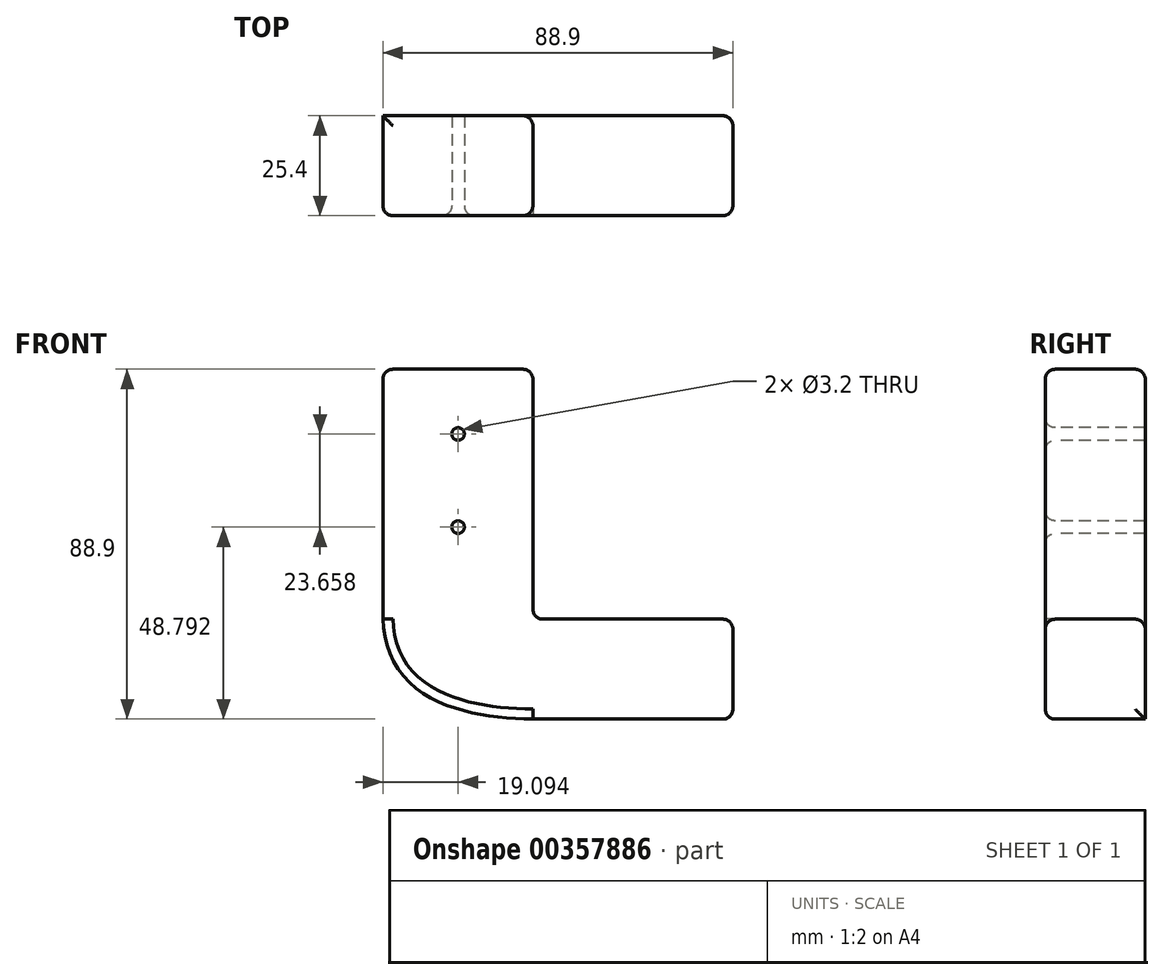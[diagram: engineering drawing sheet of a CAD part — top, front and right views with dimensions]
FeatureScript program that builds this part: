
annotation { "Feature Type Name" : "Feature", "Feature Type Description" : "" }
export const myFeature = defineFeature(function(context is Context, id is Id, definition is map)
    precondition{}
    {
        {
            var Q0;
            Q0=qCreatedBy(makeId("Front.planeOp"),FACE);
            var sketch = newSketch(context, id + "F0", { "sketchPlane" : qUnion([Q0])});
            skLineSegment(sketch, "E0.bottom", {"start": v(-38.1, 63.5) * mm, "end": v(0, 63.5) * mm});
            skLineSegment(sketch, "E0.top", {"start": v(-38.1, 0) * mm, "end": v(0, 0) * mm});
            skLineSegment(sketch, "E0.left", {"start": v(-38.1, 63.5) * mm, "end": v(-38.1, 0) * mm});
            skLineSegment(sketch, "E0.right", {"start": v(0, 63.5) * mm, "end": v(0, 0) * mm});
            skLineSegment(sketch, "E1.bottom", {"start": v(0, 0) * mm, "end": v(50.8, 0) * mm});
            skLineSegment(sketch, "E1.top", {"start": v(0, -25.4) * mm, "end": v(50.8, -25.4) * mm});
            skLineSegment(sketch, "E1.left", {"start": v(0, 0) * mm, "end": v(0, -25.4) * mm});
            skLineSegment(sketch, "E1.right", {"start": v(50.8, 0) * mm, "end": v(50.8, -25.4) * mm});
            skFitSpline(sketch, "E2", {"points": [v(-38.1, 0) * mm, v(0, -25.4) * mm], "startDerivative": vector(1.89, -52.81) * mm, "endDerivative": vector(68.37, -0.94) * mm});
            skSolve(sketch);
        }
        {
            var Q0;
            Q0 = qSketchRegion(id + "F0", true);
            extrude(context, id + "F1", {"entities" : qUnion([Q0]), "depth" : 25.4 * mm});
        }
        {
            var Q0;
            Q0=makeQuery(id+"F1.opExtrude","CAP_FACE",FACE,{"disambiguationData":[OSD([sQuery(id+"F0.wireOp",EDGE,"E0.bottom"),sQuery(id+"F0.wireOp",EDGE,"E0.left"),sQuery(id+"F0.wireOp",EDGE,"E0.right"),sQuery(id+"F0.wireOp",EDGE,"E1.bottom"),sQuery(id+"F0.wireOp",EDGE,"E1.top"),sQuery(id+"F0.wireOp",EDGE,"E1.right"),sQuery(id+"F0.wireOp",EDGE,"E2")])],"isStart":false});
            var sketch = newSketch(context, id + "F2", { "sketchPlane" : qUnion([Q0])});
            skLineSegment(sketch, "E3", {"start": v(-38.1, 63.5) * mm, "end": v(-19, 47.05) * mm});
            skLineSegment(sketch, "E4", {"start": v(-19, 47.05) * mm, "end": v(-19, 23.4) * mm});
            skSolve(sketch);
        }
        {
            var Q0;
            Q0=sQuery(id+"F2.wireOp",VERTEX,"E4.start");
            var Q1;
            Q1=sQuery(id+"F2.wireOp",VERTEX,"E4.end");
            var Q2;
            Q2=makeQuery(id+"F1.opExtrude","SWEPT_BODY",BODY,{"disambiguationData":[OSD([sQuery(id+"F0.wireOp",EDGE,"E0.bottom"),sQuery(id+"F0.wireOp",EDGE,"E0.left"),sQuery(id+"F0.wireOp",EDGE,"E0.right"),sQuery(id+"F0.wireOp",EDGE,"E1.bottom"),sQuery(id+"F0.wireOp",EDGE,"E1.top"),sQuery(id+"F0.wireOp",EDGE,"E1.right"),sQuery(id+"F0.wireOp",EDGE,"E2")])]});
            hole(context, id + "F3", {"style" : HoleStyle.SIMPLE, "endStyle" : HoleEndStyle.THROUGH, "standardTappedOrClearance" : lookupTablePath({ "standard" : "ISO", "engagement" : "75%", "pitch" : "0.75 mm", "size" : "M4", "type" : "Tapped" }), "standardBlindInLast" : lookupTablePath({ "standard" : "ISO", "engagement" : "75%", "pitch" : "0.75 mm", "size" : "M4", "type" : "Tapped" }), "holeDiameter" : 3.2 * mm, "showTappedDepth" : true, "isTappedThrough" : true, "tappedDepth" : 12.7 * mm, "tapClearance" : 3, "locations" : qUnion([Q0, Q1]), "scope" : qUnion([Q2])});
        }
        {
            var Q0;
            Q0=makeQuery(id+"F1.opExtrude","CAP_FACE",FACE,{"disambiguationData":[OSD([sQuery(id+"F0.wireOp",EDGE,"E0.bottom"),sQuery(id+"F0.wireOp",EDGE,"E0.left"),sQuery(id+"F0.wireOp",EDGE,"E0.right"),sQuery(id+"F0.wireOp",EDGE,"E1.bottom"),sQuery(id+"F0.wireOp",EDGE,"E1.top"),sQuery(id+"F0.wireOp",EDGE,"E1.right"),sQuery(id+"F0.wireOp",EDGE,"E2")])],"isStart":false});
            var Q1;
            Q1=makeQuery(id+"F1.opExtrude","SWEPT_FACE",FACE,{"disambiguationData":[OSD([sQuery(id+"F0.wireOp",EDGE,"E0.bottom")])]});
            var Q2;
            Q2=makeQuery(id+"F1.opExtrude","SWEPT_FACE",FACE,{"disambiguationData":[OSD([sQuery(id+"F0.wireOp",EDGE,"E0.right")])]});
            var Q3;
            Q3=makeQuery(id+"F1.opExtrude","CAP_EDGE",EDGE,{"disambiguationData":[OSD([sQuery(id+"F0.wireOp",EDGE,"E1.bottom")])],"isStart":true});
            var Q4;
            Q4=makeQuery(id+"F1.opExtrude","SWEPT_FACE",FACE,{"disambiguationData":[OSD([sQuery(id+"F0.wireOp",EDGE,"E1.right")])]});
            fillet(context, id + "F4", {"entities" : qUnion([Q0, Q1, Q2, Q3, Q4]), "radius" : 2.54 * mm, "tangentPropagation" : true, "allowEdgeOverflow" : false});
        }
    });
